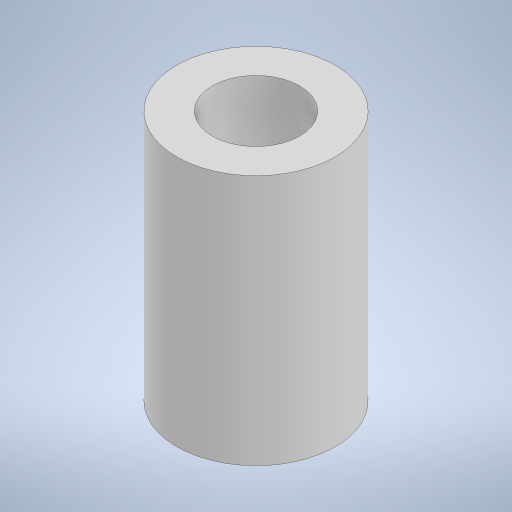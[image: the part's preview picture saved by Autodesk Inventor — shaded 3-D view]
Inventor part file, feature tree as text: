
AUTODESK INVENTOR PART (.ipt)
format: ipt  version: 2024 (Build 280153000, 153)  size: 231,936 bytes
history: native  units: mm
features: extrude x2, fillet x2, sketch x2, other x1
ambient origin geometry x8: Origin, YZ Plane, XZ Plane, XY Plane, X Axis, Y Axis, Z Axis, Center Point
bodies: Body1 (feature_tree)
feature tree (7):
  other  "Твердое тело1"
  extrude  "Выдавливание1"  Depth=25.4mm
  extrude  "Выдавливание2"  Depth=30.0mm
  fillet  "Сопряжение1"  Radius=17.5mm
  fillet  "Сопряжение2"  Radius=16.5mm
  sketch  "Эскиз1"
  sketch  "Эскиз3"
